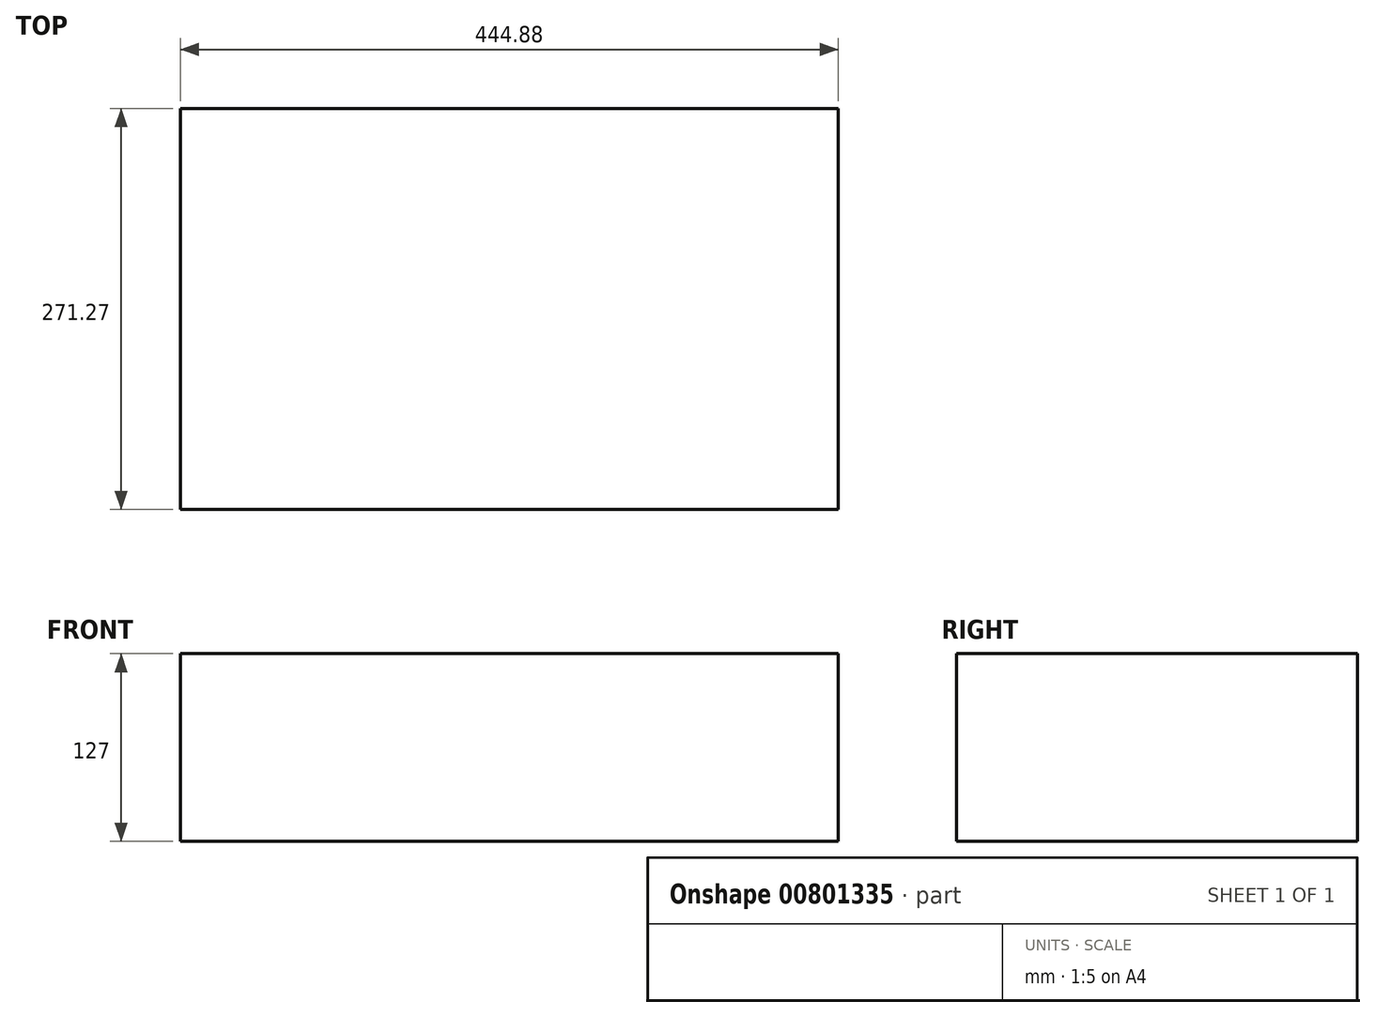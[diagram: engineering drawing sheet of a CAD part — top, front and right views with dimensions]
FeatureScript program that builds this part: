
annotation { "Feature Type Name" : "Feature", "Feature Type Description" : "" }
export const myFeature = defineFeature(function(context is Context, id is Id, definition is map)
    precondition{}
    {
        {
            var Q0;
            Q0=qCreatedBy(makeId("Front.planeOp"),FACE);
            var sketch = newSketch(context, id + "F0", { "sketchPlane" : qUnion([Q0])});
            skLineSegment(sketch, "E0.bottom", {"start": v(222.44, 63.5) * mm, "end": v(-222.44, 63.5) * mm});
            skLineSegment(sketch, "E0.top", {"start": v(222.44, -63.5) * mm, "end": v(-222.44, -63.5) * mm});
            skLineSegment(sketch, "E0.left", {"start": v(222.44, 63.5) * mm, "end": v(222.44, -63.5) * mm});
            skLineSegment(sketch, "E0.right", {"start": v(-222.44, 63.5) * mm, "end": v(-222.44, -63.5) * mm});
            skPoint(sketch, "E0.middle", {"position": v(0, 0) * mm});
            skSolve(sketch);
        }
        {
            var Q0;
            Q0 = qSketchRegion(id + "F0", true);
            extrude(context, id + "F1", {"entities" : qUnion([Q0]), "depth" : 271.27 * mm, "offsetDistance" : 25.4 * mm});
        }
    });
